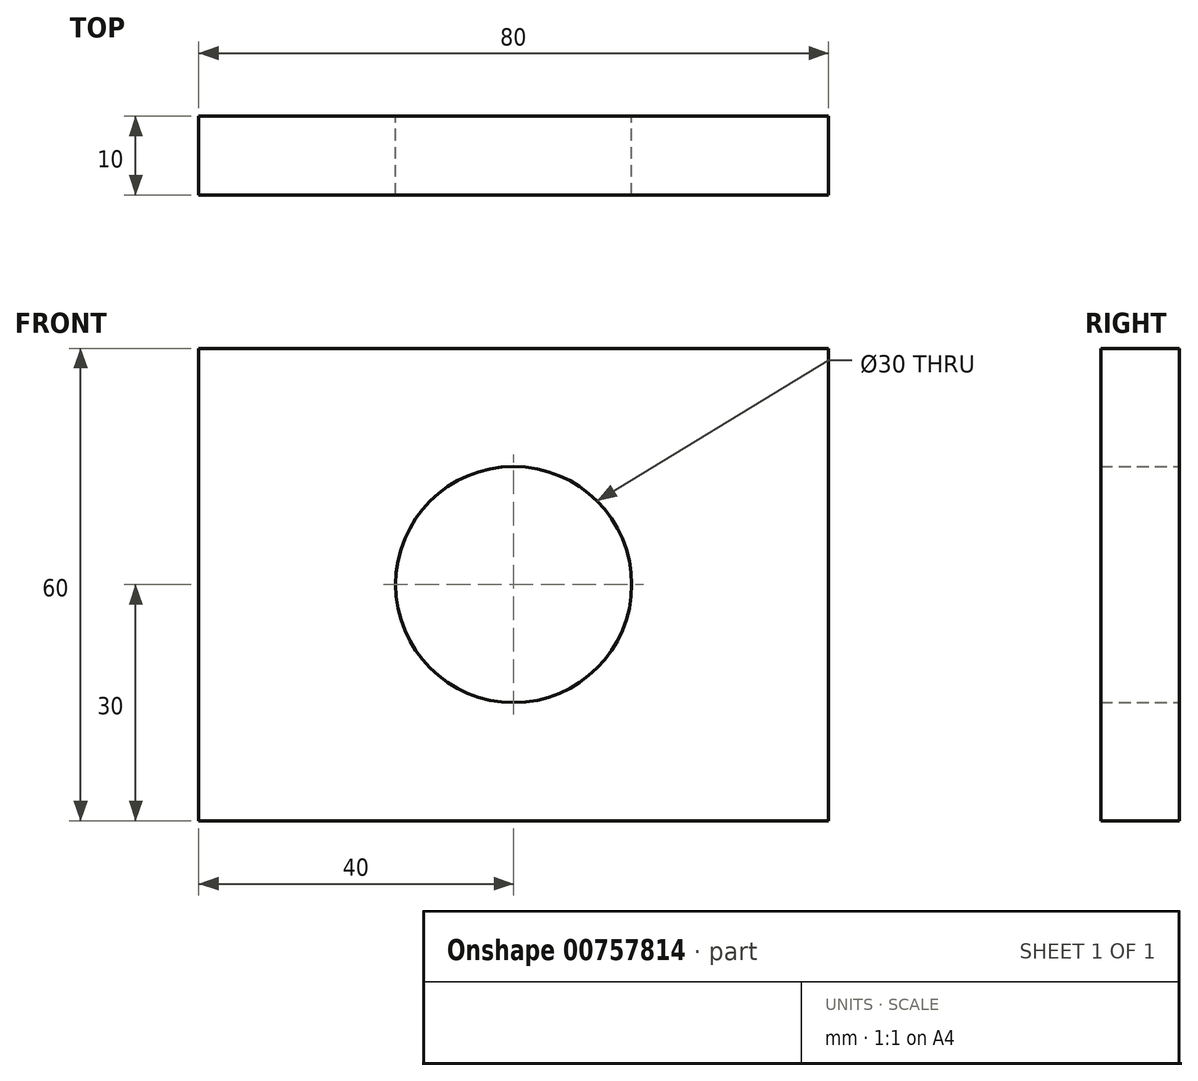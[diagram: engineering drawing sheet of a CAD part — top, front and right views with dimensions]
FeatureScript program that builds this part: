
annotation { "Feature Type Name" : "Feature", "Feature Type Description" : "" }
export const myFeature = defineFeature(function(context is Context, id is Id, definition is map)
    precondition{}
    {
        {
            var Q0;
            Q0=qCreatedBy(makeId("Front.planeOp"),FACE);
            var sketch = newSketch(context, id + "F0", { "sketchPlane" : qUnion([Q0])});
            skLineSegment(sketch, "E0.bottom", {"start": v(0, 0) * mm, "end": v(80, 0) * mm});
            skLineSegment(sketch, "E0.top", {"start": v(0, 60) * mm, "end": v(80, 60) * mm});
            skLineSegment(sketch, "E0.left", {"start": v(0, 0) * mm, "end": v(0, 60) * mm});
            skLineSegment(sketch, "E0.right", {"start": v(80, 0) * mm, "end": v(80, 60) * mm});
            skCircle(sketch, "E1", {"center": v(40, 30) * mm, "radius": 15 * mm});
            skSolve(sketch);
        }
        {
            var Q0;
            Q0=makeQuery(id+"F0.imprint","IMPRINT",FACE,{"disambiguationData":[TD([[makeQuery(id+"F0.imprint","IMPRINT",EDGE,{"derivedFrom":sQuery(id+"F0.wireOp",EDGE,"E0.bottom")}),1.0]])]});
            extrude(context, id + "F1", {"entities" : qUnion([Q0]), "depth" : 10 * mm, "offsetDistance" : 25 * mm});
        }
    });
